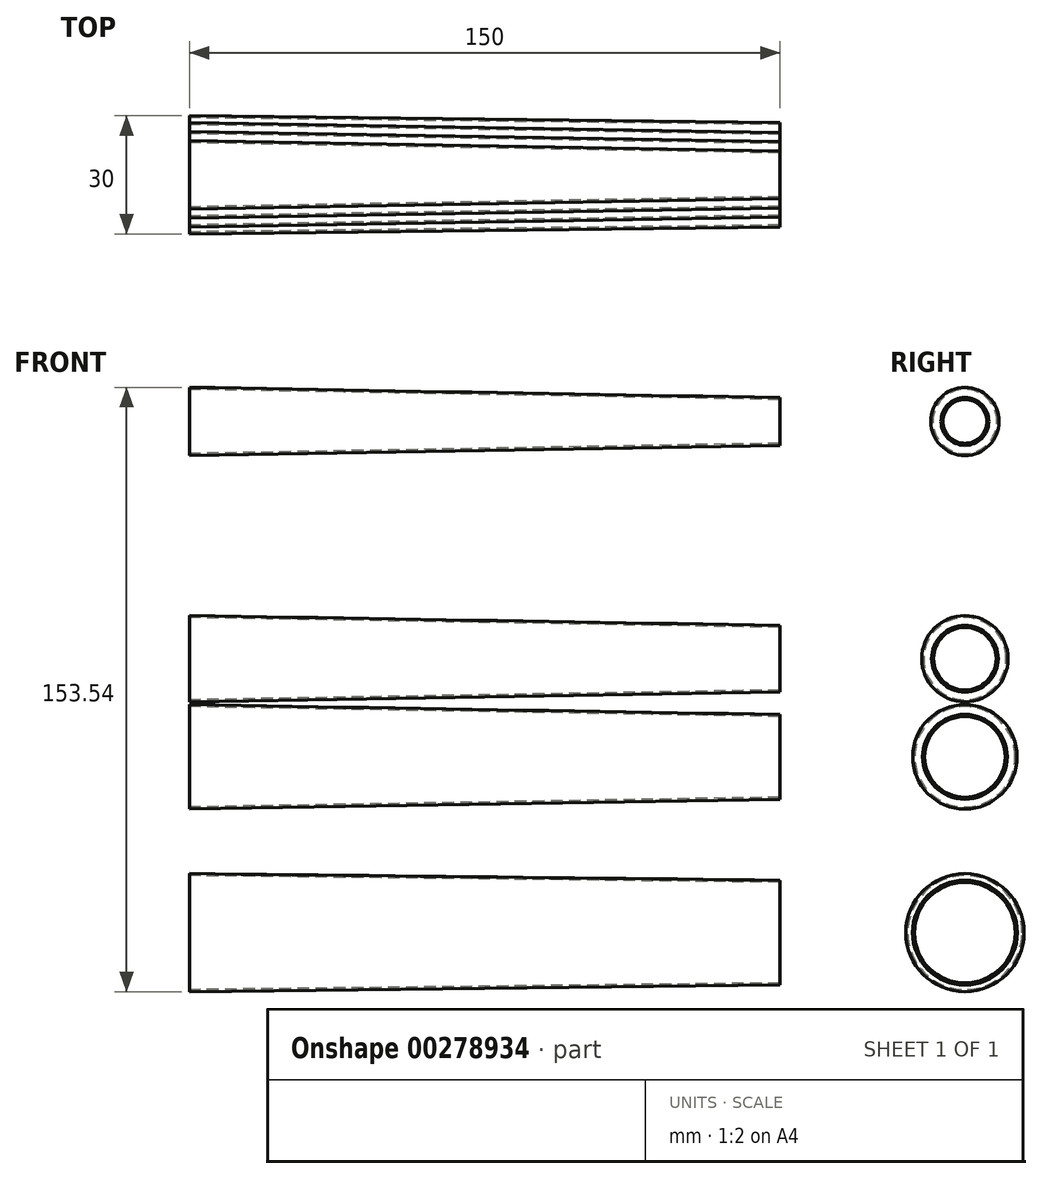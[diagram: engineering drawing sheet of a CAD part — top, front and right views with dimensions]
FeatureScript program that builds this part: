
annotation { "Feature Type Name" : "Feature", "Feature Type Description" : "" }
export const myFeature = defineFeature(function(context is Context, id is Id, definition is map)
    precondition{}
    {
        {
            var Q0;
            Q0=qCreatedBy(makeId("Front.planeOp"),FACE);
            var sketch = newSketch(context, id + "F0", { "sketchPlane" : qUnion([Q0])});
            skPoint(sketch, "E0", {"position": v(0, 14.5) * mm});
            skPoint(sketch, "E1", {"position": v(150, 12.8) * mm});
            skLineSegment(sketch, "E2", {"start": v(0, 15) * mm, "end": v(150, 13.3) * mm});
            skLineSegment(sketch, "E3", {"start": v(0, 14.5) * mm, "end": v(150, 12.8) * mm});
            skLineSegment(sketch, "E4", {"start": v(0, 15) * mm, "end": v(0, 14.5) * mm});
            skLineSegment(sketch, "E5", {"start": v(150, 13.3) * mm, "end": v(150, 12.8) * mm});
            skLineSegment(sketch, "E6", {"start": v(0, 0) * mm, "end": v(120, 0) * mm, "construction": true});
            skSolve(sketch);
        }
        {
            var Q0;
            Q0=makeQuery(id+"F0.imprint","IMPRINT",FACE,{"disambiguationData":[TD([[makeQuery(id+"F0.imprint","IMPRINT",EDGE,{"derivedFrom":sQuery(id+"F0.wireOp",EDGE,"E2")}),-1.0]])]});
            var Q1;
            Q1=sQuery(id+"F0.wireOp",EDGE,"E6");
            revolve(context, id + "F1", {"entities" : qUnion([Q0]), "axis" : qUnion([Q1]), "revolveType" : RevolveType.FULL});
        }
        {
            var Q0;
            Q0=qCreatedBy(makeId("Front.planeOp"),FACE);
            var sketch = newSketch(context, id + "F2", { "sketchPlane" : qUnion([Q0])});
            skLineSegment(sketch, "E7", {"start": v(0, 44.66) * mm, "end": v(120, 44.66) * mm, "construction": true});
            skPoint(sketch, "E8", {"position": v(0, 57.42) * mm});
            skPoint(sketch, "E9", {"position": v(150, 54.92) * mm});
            skLineSegment(sketch, "E10", {"start": v(0, 57.92) * mm, "end": v(150, 55.42) * mm});
            skLineSegment(sketch, "E11", {"start": v(0, 57.42) * mm, "end": v(150, 54.92) * mm});
            skLineSegment(sketch, "E12", {"start": v(0, 57.92) * mm, "end": v(0, 57.42) * mm});
            skLineSegment(sketch, "E13", {"start": v(150, 55.42) * mm, "end": v(150, 54.92) * mm});
            skSolve(sketch);
        }
        {
            var Q0;
            Q0=makeQuery(id+"F2.imprint","IMPRINT",FACE,{"disambiguationData":[TD([[makeQuery(id+"F2.imprint","IMPRINT",EDGE,{"derivedFrom":sQuery(id+"F2.wireOp",EDGE,"E10")}),-1.0]])]});
            var Q1;
            Q1=sQuery(id+"F2.wireOp",EDGE,"E7");
            revolve(context, id + "F3", {"entities" : qUnion([Q0]), "axis" : qUnion([Q1]), "revolveType" : RevolveType.FULL});
        }
        {
            var Q0;
            Q0=qCreatedBy(makeId("Front.planeOp"),FACE);
            var sketch = newSketch(context, id + "F4", { "sketchPlane" : qUnion([Q0])});
            skLineSegment(sketch, "E14", {"start": v(0, 69.6) * mm, "end": v(120, 69.6) * mm, "construction": true});
            skPoint(sketch, "E15", {"position": v(0, 80.06) * mm});
            skPoint(sketch, "E16", {"position": v(150, 77.56) * mm});
            skLineSegment(sketch, "E17", {"start": v(0, 80.56) * mm, "end": v(150, 78.06) * mm});
            skLineSegment(sketch, "E18", {"start": v(150, 77.56) * mm, "end": v(0, 80.06) * mm});
            skLineSegment(sketch, "E19", {"start": v(0, 80.56) * mm, "end": v(0, 80.06) * mm});
            skLineSegment(sketch, "E20", {"start": v(150, 78.06) * mm, "end": v(150, 77.56) * mm});
            skSolve(sketch);
        }
        {
            var Q0;
            Q0=makeQuery(id+"F4.imprint","IMPRINT",FACE,{"disambiguationData":[TD([[makeQuery(id+"F4.imprint","IMPRINT",EDGE,{"derivedFrom":sQuery(id+"F4.wireOp",EDGE,"E17")}),-1.0]])]});
            var Q1;
            Q1=sQuery(id+"F4.wireOp",EDGE,"E14");
            revolve(context, id + "F5", {"entities" : qUnion([Q0]), "axis" : qUnion([Q1]), "revolveType" : RevolveType.FULL});
        }
        {
            var Q0;
            Q0=qCreatedBy(makeId("Front.planeOp"),FACE);
            var sketch = newSketch(context, id + "F6", { "sketchPlane" : qUnion([Q0])});
            skLineSegment(sketch, "E21", {"start": v(0, 129.88) * mm, "end": v(120, 129.88) * mm, "construction": true});
            skPoint(sketch, "E22", {"position": v(150, 135.44) * mm});
            skPoint(sketch, "E23", {"position": v(0, 138.04) * mm});
            skLineSegment(sketch, "E24", {"start": v(0, 138.54) * mm, "end": v(150, 135.94) * mm});
            skLineSegment(sketch, "E25", {"start": v(150, 135.44) * mm, "end": v(0, 138.04) * mm});
            skLineSegment(sketch, "E26", {"start": v(0, 138.54) * mm, "end": v(0, 138.04) * mm});
            skLineSegment(sketch, "E27", {"start": v(150, 135.94) * mm, "end": v(150, 135.44) * mm});
            skSolve(sketch);
        }
        {
            var Q0;
            Q0=makeQuery(id+"F6.imprint","IMPRINT",FACE,{"disambiguationData":[TD([[makeQuery(id+"F6.imprint","IMPRINT",EDGE,{"derivedFrom":sQuery(id+"F6.wireOp",EDGE,"E24")}),-1.0]])]});
            var Q1;
            Q1=sQuery(id+"F6.wireOp",EDGE,"E21");
            revolve(context, id + "F7", {"entities" : qUnion([Q0]), "axis" : qUnion([Q1]), "revolveType" : RevolveType.FULL});
        }
    });
